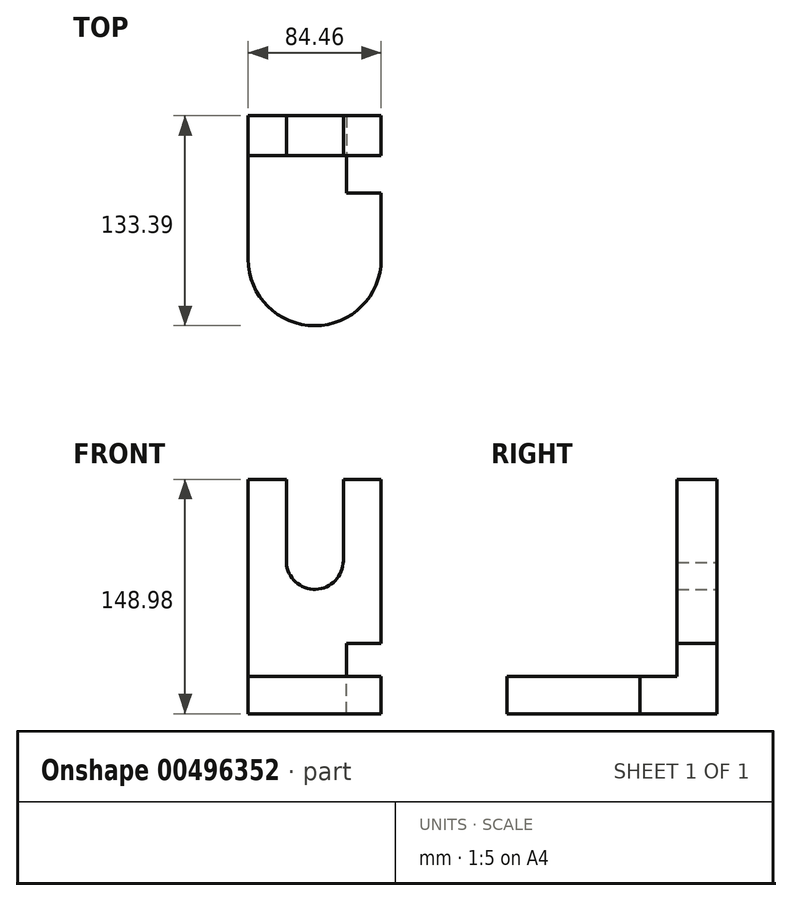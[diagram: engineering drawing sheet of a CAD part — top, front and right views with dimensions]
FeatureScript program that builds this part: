
annotation { "Feature Type Name" : "Feature", "Feature Type Description" : "" }
export const myFeature = defineFeature(function(context is Context, id is Id, definition is map)
    precondition{}
    {
        {
            var Q0;
            Q0=qCreatedBy(makeId("Front.planeOp"),FACE);
            var sketch = newSketch(context, id + "F0", { "sketchPlane" : qUnion([Q0])});
            skLineSegment(sketch, "E0.bottom", {"start": v(42.23, 74.5) * mm, "end": v(18.17, 74.5) * mm});
            skLineSegment(sketch, "E0.top", {"start": v(42.23, -74.5) * mm, "end": v(-42.23, -74.5) * mm});
            skLineSegment(sketch, "E0.left", {"start": v(42.23, 74.5) * mm, "end": v(42.23, -74.5) * mm});
            skLineSegment(sketch, "E0.right", {"start": v(-42.23, 74.5) * mm, "end": v(-42.23, -74.5) * mm});
            skPoint(sketch, "E0.middle", {"position": v(0, 0) * mm});
            skLineSegment(sketch, "E1", {"start": v(-18.07, 21.6) * mm, "end": v(-18.07, 74.5) * mm});
            skLineSegment(sketch, "E2", {"start": v(18.17, 22.74) * mm, "end": v(18.17, 74.5) * mm});
            skLineSegment(sketch, "E3.trimOffspring", {"start": v(-18.07, 74.5) * mm, "end": v(-42.23, 74.5) * mm});
            skArc(sketch, "E4", {"start": v(-18.07, 21.6) * mm, "mid": v(0.6, 4.6) * mm, "end": v(18.17, 22.74) * mm});
            skSolve(sketch);
        }
        {
            var Q0;
            {var subQ0=sQuery(id+"F0.wireOp",EDGE,"E0.bottom");Q0=makeQuery(id+"F0.imprint","IMPRINT",FACE,{"disambiguationData":[TD([[makeQuery(id+"F0.imprint","IMPRINT",EDGE,{"derivedFrom":subQ0}),1.0]])]});}
            extrude(context, id + "F1", {"entities" : qUnion([Q0]), "depth" : 25.4 * mm});
        }
        {
            var Q0;
            Q0=qCreatedBy(makeId("Top.planeOp"),FACE);
            var sketch = newSketch(context, id + "F2", { "sketchPlane" : qUnion([Q0])});
            skLineSegment(sketch, "E5.bottom", {"start": v(42.23, 0) * mm, "end": v(-42.23, 0) * mm});
            skLineSegment(sketch, "E5.left", {"start": v(42.23, 0) * mm, "end": v(42.23, -91.16) * mm});
            skLineSegment(sketch, "E5.right", {"start": v(-42.23, 0) * mm, "end": v(-42.23, -91.16) * mm});
            skPoint(sketch, "E5.middle", {"position": v(0, -45.58) * mm});
            skArc(sketch, "E6", {"start": v(-42.23, -91.16) * mm, "mid": v(0, -133.39) * mm, "end": v(42.23, -91.16) * mm});
            skSolve(sketch);
        }
        {
            var Q0;
            Q0=makeQuery(id+"F2.imprint","IMPRINT",FACE,{"disambiguationData":[TD([[makeQuery(id+"F2.imprint","IMPRINT",EDGE,{"derivedFrom":sQuery(id+"F2.wireOp",EDGE,"E5.bottom")}),1.0]])]});
            var Q1;
            Q1=makeQuery(id+"F1.opExtrude","SWEPT_FACE",FACE,{"disambiguationData":[OSD([sQuery(id+"F0.wireOp",EDGE,"E0.top")])]});
            var Q2;
            Q2=makeQuery(id+"F1.opExtrude","SWEPT_FACE",FACE,{"disambiguationData":[OSD([sQuery(id+"F0.wireOp",EDGE,"E3.trimOffspring")])]});
            extrude(context, id + "F3", {"entities" : qUnion([Q0]), "operationType" : NewBodyOperationType.ADD, "endBound" : BoundingType.UP_TO_SURFACE, "oppositeDirection" : true, "endBoundEntityFace" : qUnion([Q1]), "depth" : 25.4 * mm, "hasSecondDirection" : true, "secondDirectionOppositeDirection" : true, "secondDirectionBoundEntityFace" : qUnion([Q2]), "secondDirectionDepth" : 50.8 * mm});
        }
        {
            var Q0;
            Q0=qCreatedBy(makeId("Right.planeOp"),FACE);
            var sketch = newSketch(context, id + "F4", { "sketchPlane" : qUnion([Q0])});
            skLineSegment(sketch, "E7.bottom", {"start": v(12.7, -87.87) * mm, "end": v(-49.16, -87.87) * mm});
            skLineSegment(sketch, "E7.top", {"start": v(12.7, -29.86) * mm, "end": v(-49.16, -29.86) * mm});
            skLineSegment(sketch, "E7.left", {"start": v(12.7, -87.87) * mm, "end": v(12.7, -29.86) * mm});
            skLineSegment(sketch, "E7.right", {"start": v(-49.16, -87.87) * mm, "end": v(-49.16, -29.86) * mm});
            skSolve(sketch);
        }
        {
            var Q0;
            Q0=makeQuery(id+"F4.imprint","IMPRINT",FACE,{"disambiguationData":[TD([[makeQuery(id+"F4.imprint","IMPRINT",EDGE,{"derivedFrom":sQuery(id+"F4.wireOp",EDGE,"E7.bottom")}),-1.0]])]});
            var Q1;
            Q1=makeQuery(id+"F3.boolean.opBoolean","MERGE",FACE,{"derivedFrom":[makeQuery(id+"F1.opExtrude","SWEPT_FACE",FACE,{"disambiguationData":[OSD([sQuery(id+"F0.wireOp",EDGE,"E0.left")])]}),makeQuery(id+"F3.opExtrude","SWEPT_FACE",FACE,{"disambiguationData":[OSD([sQuery(id+"F2.wireOp",EDGE,"E5.left")])]})]});
            extrude(context, id + "F5", {"entities" : qUnion([Q0]), "operationType" : NewBodyOperationType.REMOVE, "endBound" : BoundingType.UP_TO_SURFACE, "endBoundEntityFace" : qUnion([Q1]), "depth" : 25.4 * mm, "hasSecondDirection" : true, "secondDirectionOppositeDirection" : false, "secondDirectionDepth" : 20.32 * mm});
        }
    });
